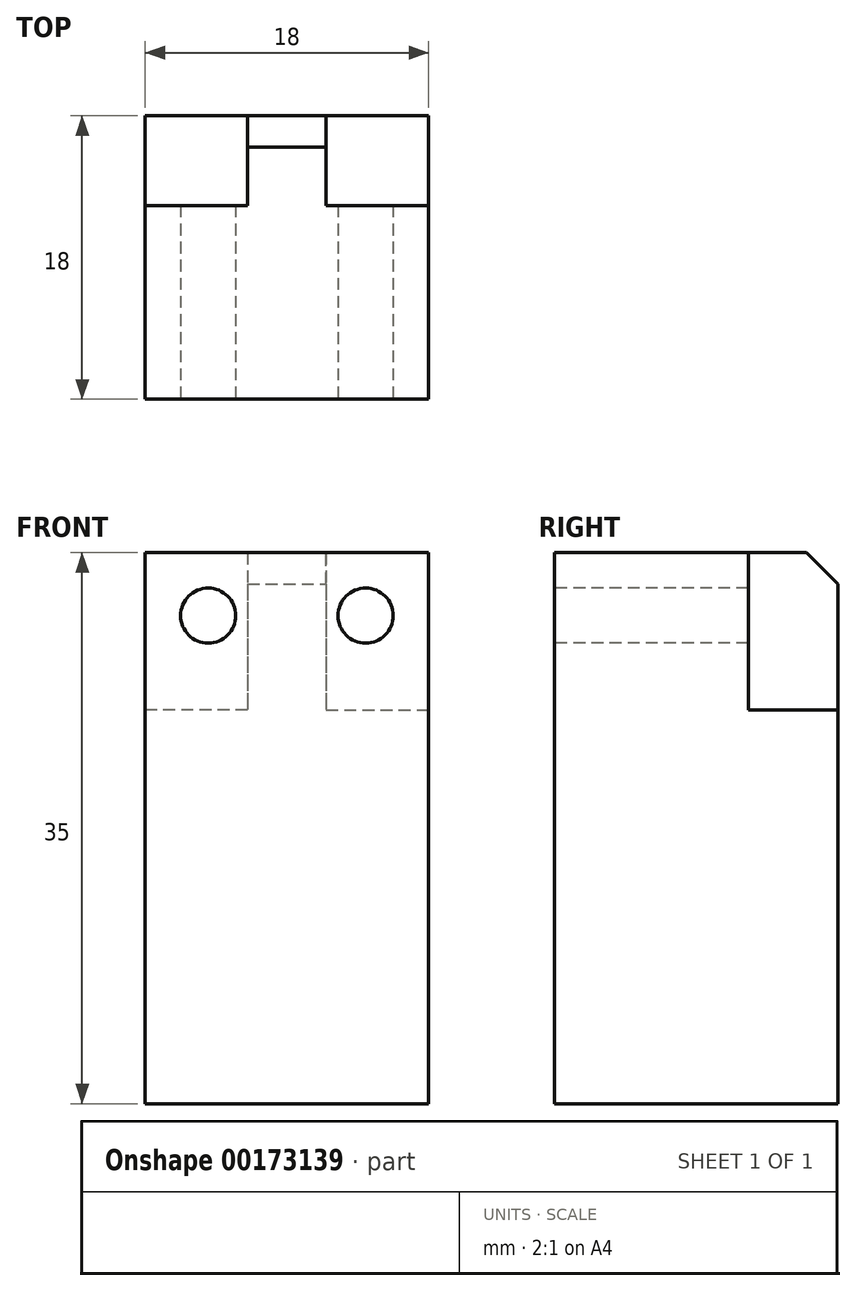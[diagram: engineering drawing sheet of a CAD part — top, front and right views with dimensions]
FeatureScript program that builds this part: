
annotation { "Feature Type Name" : "Feature", "Feature Type Description" : "" }
export const myFeature = defineFeature(function(context is Context, id is Id, definition is map)
    precondition{}
    {
        {
            var Q0;
            Q0=qCreatedBy(makeId("Top.planeOp"),FACE);
            var sketch = newSketch(context, id + "F0", { "sketchPlane" : qUnion([Q0])});
            skLineSegment(sketch, "E0.bottom", {"start": v(-9, 9) * mm, "end": v(9, 9) * mm});
            skLineSegment(sketch, "E0.top", {"start": v(-9, -9) * mm, "end": v(9, -9) * mm});
            skLineSegment(sketch, "E0.left", {"start": v(-9, 9) * mm, "end": v(-9, -9) * mm});
            skLineSegment(sketch, "E0.right", {"start": v(9, 9) * mm, "end": v(9, -9) * mm});
            skPoint(sketch, "E1", {"position": v(0, 9) * mm});
            skPoint(sketch, "E2", {"position": v(9, 0) * mm});
            skLineSegment(sketch, "E3", {"start": v(-2.5, 9) * mm, "end": v(-2.5, 3.3) * mm});
            skLineSegment(sketch, "E4", {"start": v(2.5, 3.3) * mm, "end": v(2.5, 9) * mm});
            skLineSegment(sketch, "E5", {"start": v(-2.5, 3.3) * mm, "end": v(-9, 3.3) * mm});
            skLineSegment(sketch, "E6", {"start": v(2.5, 3.3) * mm, "end": v(9, 3.3) * mm});
            skSolve(sketch);
        }
        {
            var Q0;
            {var subQ1=sQuery(id+"F0.wireOp",EDGE,"E0.top");Q0=makeQuery(id+"F0.imprint","IMPRINT",FACE,{"disambiguationData":[TD([[makeQuery(id+"F0.imprint","IMPRINT",EDGE,{"derivedFrom":subQ1}),1.0]])]});}
            var Q1;
            {var subQ3=sQuery(id+"F0.wireOp",EDGE,"E3");Q1=makeQuery(id+"F0.imprint","IMPRINT",FACE,{"disambiguationData":[TD([[makeQuery(id+"F0.imprint","IMPRINT",EDGE,{"derivedFrom":subQ3}),-1.0]])]});}
            var Q2;
            {var subQ3=sQuery(id+"F0.wireOp",EDGE,"E4");Q2=makeQuery(id+"F0.imprint","IMPRINT",FACE,{"disambiguationData":[TD([[makeQuery(id+"F0.imprint","IMPRINT",EDGE,{"derivedFrom":subQ3}),-1.0]])]});}
            extrude(context, id + "F1", {"entities" : qUnion([Q0, Q1, Q2]), "oppositeDirection" : true, "depth" : 25 * mm});
        }
        {
            var Q0;
            {var subQ1=sQuery(id+"F0.wireOp",EDGE,"E0.top");Q0=makeQuery(id+"F0.imprint","IMPRINT",FACE,{"disambiguationData":[TD([[makeQuery(id+"F0.imprint","IMPRINT",EDGE,{"derivedFrom":subQ1}),1.0]])]});}
            extrude(context, id + "F2", {"entities" : qUnion([Q0]), "operationType" : NewBodyOperationType.ADD, "depth" : 10 * mm});
        }
        {
            var Q0;
            Q0=makeQuery(id+"F2.opExtrude","CAP_EDGE",EDGE,{"disambiguationData":[OSD([sQuery(id+"F0.wireOp",EDGE,"E0.bottom")])],"isStart":false});
            chamfer(context, id + "F3", {"entities" : qUnion([Q0]), "width" : 2 * mm, "tangentPropagation" : true});
        }
        {
            var Q0;
            {var subQ0=sQuery(id+"F0.wireOp",EDGE,"E0.top");Q0=makeQuery(id+"F2.boolean.opBoolean","MERGE",FACE,{"derivedFrom":[makeQuery(id+"F1.opExtrude","SWEPT_FACE",FACE,{"disambiguationData":[OSD([subQ0])]}),makeQuery(id+"F2.opExtrude","SWEPT_FACE",FACE,{"disambiguationData":[OSD([subQ0])]})]});}
            var sketch = newSketch(context, id + "F4", { "sketchPlane" : qUnion([Q0])});
            skLineSegment(sketch, "E7.0", {"start": v(-9, 10) * mm, "end": v(9, 10) * mm, "construction": true});
            skPoint(sketch, "E8", {"position": v(-5, 6) * mm});
            skLineSegment(sketch, "E9", {"start": v(-9, 10) * mm, "end": v(-9, -12.62) * mm, "construction": true});
            skPoint(sketch, "E10.MirrorP", {"position": v(5, 6) * mm});
            skSolve(sketch);
        }
        {
            var Q0;
            Q0=sQuery(id+"F4.wireOp",VERTEX,"E8");
            var Q1;
            Q1=sQuery(id+"F4.wireOp",VERTEX,"E10.MirrorP");
            var Q2;
            Q2=makeQuery(id+"F1.opExtrude","SWEPT_BODY",BODY,{"disambiguationData":[OSD([sQuery(id+"F0.wireOp",EDGE,"E0.bottom"),sQuery(id+"F0.wireOp",EDGE,"E0.top"),sQuery(id+"F0.wireOp",EDGE,"E0.left"),sQuery(id+"F0.wireOp",EDGE,"E0.right")])]});
            hole(context, id + "F5", {"style" : HoleStyle.SIMPLE, "endStyle" : HoleEndStyle.THROUGH, "holeDiameter" : 3.5 * mm, "startFromSketch" : true, "locations" : qUnion([Q0, Q1]), "scope" : qUnion([Q2]), "isTappedThrough" : true});
        }
    });
